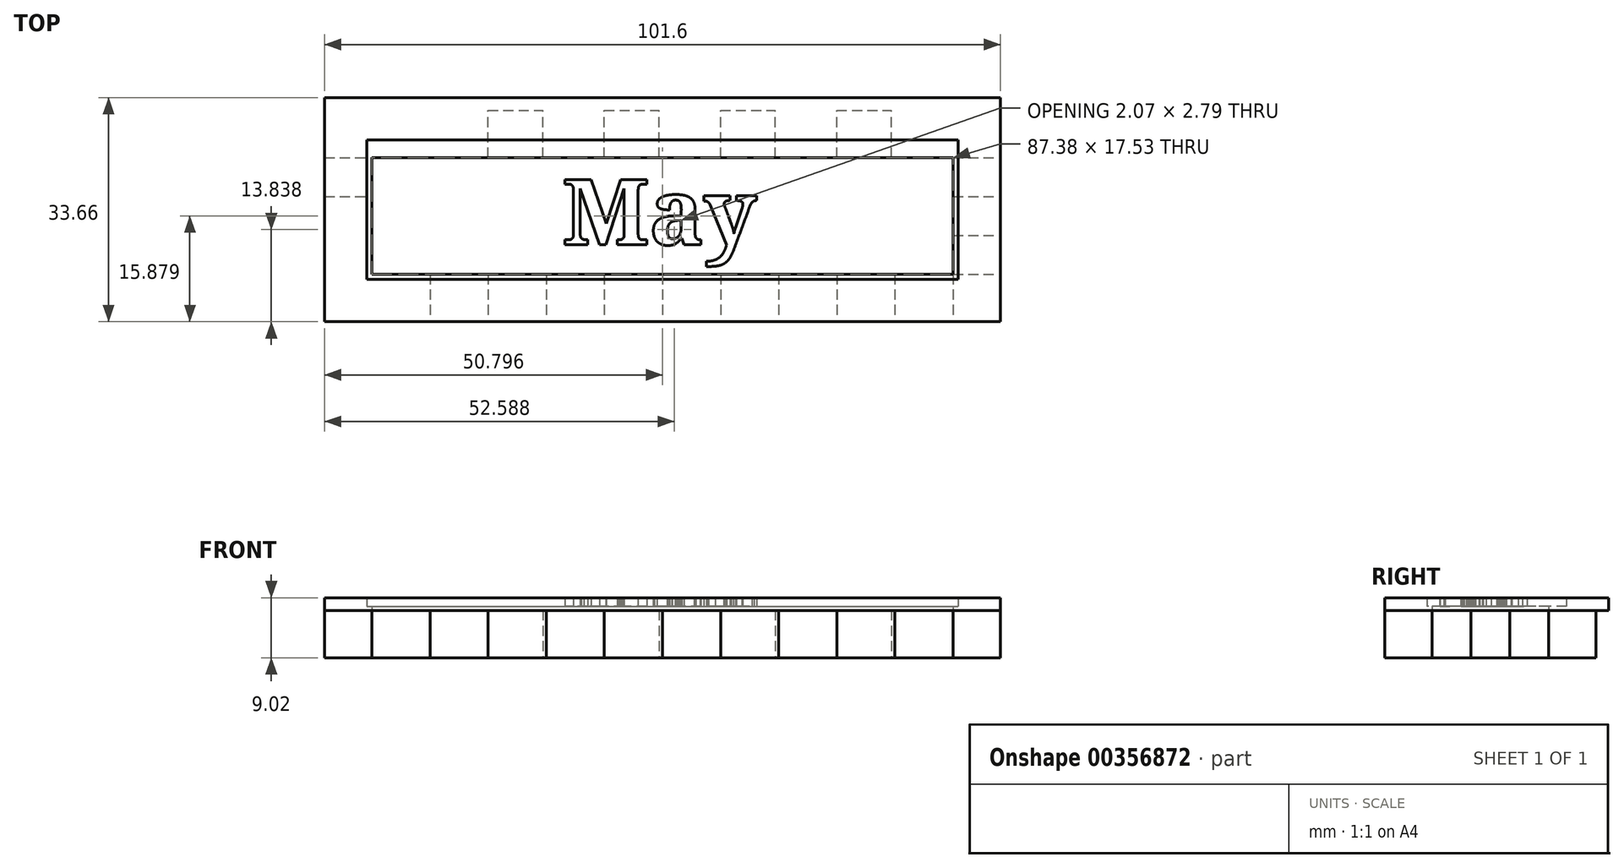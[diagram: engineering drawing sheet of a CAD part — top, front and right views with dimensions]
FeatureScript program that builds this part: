
annotation { "Feature Type Name" : "Feature", "Feature Type Description" : "" }
export const myFeature = defineFeature(function(context is Context, id is Id, definition is map)
    precondition{}
    {
        {
            var Q0;
            Q0=qCreatedBy(makeId("Top.planeOp"),FACE);
            var sketch = newSketch(context, id + "F0", { "sketchPlane" : qUnion([Q0])});
            skLineSegment(sketch, "E0.bottom", {"start": v(-52.12, 11.37) * mm, "end": v(49.48, 11.37) * mm});
            skLineSegment(sketch, "E0.top", {"start": v(-52.12, -20.38) * mm, "end": v(49.48, -20.38) * mm});
            skLineSegment(sketch, "E0.left", {"start": v(-52.12, 11.37) * mm, "end": v(-52.12, -20.38) * mm});
            skLineSegment(sketch, "E0.right", {"start": v(49.48, 11.37) * mm, "end": v(49.48, -20.38) * mm});
            skLineSegment(sketch, "E1.bottom", {"start": v(-52.12, 11.37) * mm, "end": v(-45.01, 11.37) * mm});
            skLineSegment(sketch, "E1.top", {"start": v(-52.12, 4.26) * mm, "end": v(-45.01, 4.26) * mm});
            skLineSegment(sketch, "E1.left", {"start": v(-52.12, 11.37) * mm, "end": v(-52.12, 4.26) * mm});
            skLineSegment(sketch, "E1.right", {"start": v(-45.01, 11.37) * mm, "end": v(-45.01, 4.26) * mm});
            skLineSegment(sketch, "E2.bottom", {"start": v(-45.01, 11.37) * mm, "end": v(-36.78, 11.37) * mm});
            skLineSegment(sketch, "E2.top", {"start": v(-45.01, 4.26) * mm, "end": v(-36.78, 4.26) * mm});
            skLineSegment(sketch, "E2.right", {"start": v(-36.78, 11.37) * mm, "end": v(-36.78, 4.26) * mm});
            skLineSegment(sketch, "E3.bottom", {"start": v(-36.78, 4.26) * mm, "end": v(-27.54, 4.26) * mm});
            skLineSegment(sketch, "E3.top", {"start": v(-36.78, 11.37) * mm, "end": v(-27.54, 11.37) * mm});
            skLineSegment(sketch, "E3.left", {"start": v(-36.78, 4.26) * mm, "end": v(-36.78, 11.37) * mm});
            skLineSegment(sketch, "E3.right", {"start": v(-27.54, 4.26) * mm, "end": v(-27.54, 11.37) * mm});
            skLineSegment(sketch, "E4.bottom", {"start": v(-27.54, 4.26) * mm, "end": v(-19.3, 4.26) * mm});
            skLineSegment(sketch, "E4.top", {"start": v(-27.54, 11.37) * mm, "end": v(-19.3, 11.37) * mm});
            skLineSegment(sketch, "E4.right", {"start": v(-19.3, 4.26) * mm, "end": v(-19.3, 11.37) * mm});
            skLineSegment(sketch, "E5.bottom", {"start": v(-19.3, 4.26) * mm, "end": v(-10.06, 4.26) * mm});
            skLineSegment(sketch, "E5.top", {"start": v(-19.3, 11.37) * mm, "end": v(-10.06, 11.37) * mm});
            skLineSegment(sketch, "E5.right", {"start": v(-10.06, 4.26) * mm, "end": v(-10.06, 11.37) * mm});
            skLineSegment(sketch, "E6.bottom", {"start": v(-10.06, 4.26) * mm, "end": v(-10.06, 4.26) * mm});
            skLineSegment(sketch, "E6.top", {"start": v(-10.06, 11.37) * mm, "end": v(-10.06, 11.37) * mm});
            skLineSegment(sketch, "E7.bottom", {"start": v(-10.06, 4.26) * mm, "end": v(-1.83, 4.26) * mm});
            skLineSegment(sketch, "E7.top", {"start": v(-10.06, 11.37) * mm, "end": v(-1.83, 11.37) * mm});
            skLineSegment(sketch, "E7.right", {"start": v(-1.83, 4.26) * mm, "end": v(-1.83, 11.37) * mm});
            skLineSegment(sketch, "E8.bottom", {"start": v(-1.83, 4.26) * mm, "end": v(7.41, 4.26) * mm});
            skLineSegment(sketch, "E8.top", {"start": v(-1.83, 11.37) * mm, "end": v(7.41, 11.37) * mm});
            skLineSegment(sketch, "E8.right", {"start": v(7.41, 4.26) * mm, "end": v(7.41, 11.37) * mm});
            skLineSegment(sketch, "E9.bottom", {"start": v(7.41, 4.26) * mm, "end": v(15.64, 4.26) * mm});
            skLineSegment(sketch, "E9.top", {"start": v(7.41, 11.37) * mm, "end": v(15.64, 11.37) * mm});
            skLineSegment(sketch, "E9.right", {"start": v(15.64, 4.26) * mm, "end": v(15.64, 11.37) * mm});
            skLineSegment(sketch, "E10.bottom", {"start": v(15.64, 4.26) * mm, "end": v(24.89, 4.26) * mm});
            skLineSegment(sketch, "E10.top", {"start": v(15.64, 11.37) * mm, "end": v(24.89, 11.37) * mm});
            skLineSegment(sketch, "E10.right", {"start": v(24.89, 4.26) * mm, "end": v(24.89, 11.37) * mm});
            skLineSegment(sketch, "E11.bottom", {"start": v(24.89, 4.26) * mm, "end": v(24.89, 4.26) * mm});
            skLineSegment(sketch, "E11.top", {"start": v(24.89, 11.37) * mm, "end": v(24.89, 11.37) * mm});
            skLineSegment(sketch, "E12.bottom", {"start": v(24.89, 4.26) * mm, "end": v(33.12, 4.26) * mm});
            skLineSegment(sketch, "E12.top", {"start": v(24.89, 11.37) * mm, "end": v(33.12, 11.37) * mm});
            skLineSegment(sketch, "E12.right", {"start": v(33.12, 4.26) * mm, "end": v(33.12, 11.37) * mm});
            skLineSegment(sketch, "E13.bottom", {"start": v(33.12, 4.26) * mm, "end": v(42.36, 4.26) * mm});
            skLineSegment(sketch, "E13.top", {"start": v(33.12, 11.37) * mm, "end": v(42.36, 11.37) * mm});
            skLineSegment(sketch, "E13.right", {"start": v(42.36, 4.26) * mm, "end": v(42.36, 11.37) * mm});
            skLineSegment(sketch, "E14.bottom", {"start": v(42.36, 4.26) * mm, "end": v(49.48, 4.26) * mm});
            skLineSegment(sketch, "E14.top", {"start": v(42.36, 11.37) * mm, "end": v(49.48, 11.37) * mm});
            skLineSegment(sketch, "E14.right", {"start": v(49.48, 4.26) * mm, "end": v(49.48, 11.37) * mm});
            skLineSegment(sketch, "E15.bottom", {"start": v(-52.12, -20.38) * mm, "end": v(-45.01, -20.38) * mm});
            skLineSegment(sketch, "E15.top", {"start": v(-52.12, -13.26) * mm, "end": v(-45.01, -13.26) * mm});
            skLineSegment(sketch, "E15.left", {"start": v(-52.12, -20.38) * mm, "end": v(-52.12, -13.26) * mm});
            skLineSegment(sketch, "E15.right", {"start": v(-45.01, -20.38) * mm, "end": v(-45.01, -13.26) * mm});
            skLineSegment(sketch, "E16.bottom", {"start": v(-45.01, -13.26) * mm, "end": v(-45.01, -13.26) * mm});
            skLineSegment(sketch, "E16.top", {"start": v(-45.01, -20.38) * mm, "end": v(-45.01, -20.38) * mm});
            skLineSegment(sketch, "E16.left", {"start": v(-45.01, -13.26) * mm, "end": v(-45.01, -20.38) * mm});
            skLineSegment(sketch, "E16.right", {"start": v(-45.01, -13.26) * mm, "end": v(-45.01, -20.38) * mm});
            skLineSegment(sketch, "E17.bottom", {"start": v(-45.01, -13.26) * mm, "end": v(-36.27, -13.26) * mm});
            skLineSegment(sketch, "E17.top", {"start": v(-45.01, -20.38) * mm, "end": v(-36.27, -20.38) * mm});
            skLineSegment(sketch, "E17.right", {"start": v(-36.27, -13.26) * mm, "end": v(-36.27, -20.38) * mm});
            skLineSegment(sketch, "E18.bottom", {"start": v(-36.27, -13.26) * mm, "end": v(-36.27, -13.26) * mm});
            skLineSegment(sketch, "E18.top", {"start": v(-36.27, -20.38) * mm, "end": v(-36.27, -20.38) * mm});
            skLineSegment(sketch, "E19.bottom", {"start": v(-36.27, -13.26) * mm, "end": v(-27.54, -13.26) * mm});
            skLineSegment(sketch, "E19.top", {"start": v(-36.27, -20.38) * mm, "end": v(-27.54, -20.38) * mm});
            skLineSegment(sketch, "E19.right", {"start": v(-27.54, -13.26) * mm, "end": v(-27.54, -20.38) * mm});
            skLineSegment(sketch, "E20.bottom", {"start": v(-27.54, -13.26) * mm, "end": v(-18.8, -13.26) * mm});
            skLineSegment(sketch, "E20.top", {"start": v(-27.54, -20.38) * mm, "end": v(-18.8, -20.38) * mm});
            skLineSegment(sketch, "E20.right", {"start": v(-18.8, -13.26) * mm, "end": v(-18.8, -20.38) * mm});
            skLineSegment(sketch, "E21.bottom", {"start": v(-18.8, -13.26) * mm, "end": v(-10.06, -13.26) * mm});
            skLineSegment(sketch, "E21.top", {"start": v(-18.8, -20.38) * mm, "end": v(-10.06, -20.38) * mm});
            skLineSegment(sketch, "E21.right", {"start": v(-10.06, -13.26) * mm, "end": v(-10.06, -20.38) * mm});
            skLineSegment(sketch, "E22.bottom", {"start": v(-10.06, -13.26) * mm, "end": v(-1.32, -13.26) * mm});
            skLineSegment(sketch, "E22.top", {"start": v(-10.06, -20.38) * mm, "end": v(-1.32, -20.38) * mm});
            skLineSegment(sketch, "E22.right", {"start": v(-1.32, -13.26) * mm, "end": v(-1.32, -20.38) * mm});
            skLineSegment(sketch, "E23.bottom", {"start": v(-1.32, -13.26) * mm, "end": v(7.41, -13.26) * mm});
            skLineSegment(sketch, "E23.top", {"start": v(-1.32, -20.38) * mm, "end": v(7.41, -20.38) * mm});
            skLineSegment(sketch, "E23.right", {"start": v(7.41, -13.26) * mm, "end": v(7.41, -20.38) * mm});
            skLineSegment(sketch, "E24.bottom", {"start": v(7.41, -13.26) * mm, "end": v(16.15, -13.26) * mm});
            skLineSegment(sketch, "E24.top", {"start": v(7.41, -20.38) * mm, "end": v(16.15, -20.38) * mm});
            skLineSegment(sketch, "E24.right", {"start": v(16.15, -13.26) * mm, "end": v(16.15, -20.38) * mm});
            skLineSegment(sketch, "E25.bottom", {"start": v(16.15, -13.26) * mm, "end": v(24.89, -13.26) * mm});
            skLineSegment(sketch, "E25.top", {"start": v(16.15, -20.38) * mm, "end": v(24.89, -20.38) * mm});
            skLineSegment(sketch, "E25.right", {"start": v(24.89, -13.26) * mm, "end": v(24.89, -20.38) * mm});
            skLineSegment(sketch, "E26.bottom", {"start": v(24.89, -13.26) * mm, "end": v(33.63, -13.26) * mm});
            skLineSegment(sketch, "E26.top", {"start": v(24.89, -20.38) * mm, "end": v(33.63, -20.38) * mm});
            skLineSegment(sketch, "E26.right", {"start": v(33.63, -13.26) * mm, "end": v(33.63, -20.38) * mm});
            skLineSegment(sketch, "E27.bottom", {"start": v(33.63, -13.26) * mm, "end": v(42.36, -13.26) * mm});
            skLineSegment(sketch, "E27.top", {"start": v(33.63, -20.38) * mm, "end": v(42.36, -20.38) * mm});
            skLineSegment(sketch, "E27.right", {"start": v(42.36, -13.26) * mm, "end": v(42.36, -20.38) * mm});
            skLineSegment(sketch, "E28.bottom", {"start": v(42.36, -13.26) * mm, "end": v(49.48, -13.26) * mm});
            skLineSegment(sketch, "E28.top", {"start": v(42.36, -20.38) * mm, "end": v(49.48, -20.38) * mm});
            skLineSegment(sketch, "E28.right", {"start": v(49.48, -13.26) * mm, "end": v(49.48, -20.38) * mm});
            skLineSegment(sketch, "E29.top", {"start": v(-52.12, -1.58) * mm, "end": v(-45.01, -1.58) * mm});
            skLineSegment(sketch, "E29.left", {"start": v(-52.12, 4.26) * mm, "end": v(-52.12, -1.58) * mm});
            skLineSegment(sketch, "E29.right", {"start": v(-45.01, 4.26) * mm, "end": v(-45.01, -1.58) * mm});
            skLineSegment(sketch, "E30.top", {"start": v(-52.12, -7.42) * mm, "end": v(-45.01, -7.42) * mm});
            skLineSegment(sketch, "E30.left", {"start": v(-52.12, -1.58) * mm, "end": v(-52.12, -7.42) * mm});
            skLineSegment(sketch, "E30.right", {"start": v(-45.01, -1.58) * mm, "end": v(-45.01, -7.42) * mm});
            skLineSegment(sketch, "E31.bottom", {"start": v(-45.01, -7.42) * mm, "end": v(-52.12, -7.42) * mm});
            skLineSegment(sketch, "E31.top", {"start": v(-45.01, -13.26) * mm, "end": v(-52.12, -13.26) * mm});
            skLineSegment(sketch, "E31.left", {"start": v(-45.01, -7.42) * mm, "end": v(-45.01, -13.26) * mm});
            skLineSegment(sketch, "E31.right", {"start": v(-52.12, -7.42) * mm, "end": v(-52.12, -13.26) * mm});
            skLineSegment(sketch, "E32.top", {"start": v(42.36, -1.58) * mm, "end": v(49.48, -1.58) * mm});
            skLineSegment(sketch, "E32.left", {"start": v(42.36, 4.26) * mm, "end": v(42.36, -1.58) * mm});
            skLineSegment(sketch, "E32.right", {"start": v(49.48, 4.26) * mm, "end": v(49.48, -1.58) * mm});
            skLineSegment(sketch, "E33.top", {"start": v(42.36, -7.42) * mm, "end": v(49.48, -7.42) * mm});
            skLineSegment(sketch, "E33.left", {"start": v(42.36, -1.58) * mm, "end": v(42.36, -7.42) * mm});
            skLineSegment(sketch, "E33.right", {"start": v(49.48, -1.58) * mm, "end": v(49.48, -7.42) * mm});
            skLineSegment(sketch, "E34.left", {"start": v(42.36, -7.42) * mm, "end": v(42.36, -13.26) * mm});
            skLineSegment(sketch, "E34.right", {"start": v(49.48, -7.42) * mm, "end": v(49.48, -13.26) * mm});
            skSolve(sketch);
        }
        {
            var Q0;
            Q0=makeQuery(id+"F0.imprint","IMPRINT",FACE,{"disambiguationData":[TD([[makeQuery(id+"F0.imprint","IMPRINT",EDGE,{"derivedFrom":sQuery(id+"F0.wireOp",EDGE,"E2.top")}),-1.0]])]});
            var Q1;
            Q1=makeQuery(id+"F0.imprint","IMPRINT",FACE,{"disambiguationData":[TD([[makeQuery(id+"F0.imprint","IMPRINT",EDGE,{"derivedFrom":sQuery(id+"F0.wireOp",EDGE,"E2.bottom")}),-1.0]])]});
            var Q2;
            Q2=makeQuery(id+"F0.imprint","IMPRINT",FACE,{"disambiguationData":[TD([[makeQuery(id+"F0.imprint","IMPRINT",EDGE,{"derivedFrom":sQuery(id+"F0.wireOp",EDGE,"E4.bottom")}),1.0]])]});
            var Q3;
            Q3=makeQuery(id+"F0.imprint","IMPRINT",FACE,{"disambiguationData":[TD([[makeQuery(id+"F0.imprint","IMPRINT",EDGE,{"derivedFrom":sQuery(id+"F0.wireOp",EDGE,"E7.bottom")}),1.0]])]});
            var Q4;
            Q4=makeQuery(id+"F0.imprint","IMPRINT",FACE,{"disambiguationData":[TD([[makeQuery(id+"F0.imprint","IMPRINT",EDGE,{"derivedFrom":sQuery(id+"F0.wireOp",EDGE,"E9.bottom")}),1.0]])]});
            var Q5;
            Q5=makeQuery(id+"F0.imprint","IMPRINT",FACE,{"disambiguationData":[TD([[makeQuery(id+"F0.imprint","IMPRINT",EDGE,{"derivedFrom":sQuery(id+"F0.wireOp",EDGE,"E12.bottom")}),1.0]])]});
            var Q6;
            Q6=makeQuery(id+"F0.imprint","IMPRINT",FACE,{"disambiguationData":[TD([[makeQuery(id+"F0.imprint","IMPRINT",EDGE,{"derivedFrom":sQuery(id+"F0.wireOp",EDGE,"E14.bottom")}),-1.0]])]});
            var Q7;
            Q7=makeQuery(id+"F0.imprint","IMPRINT",FACE,{"disambiguationData":[TD([[makeQuery(id+"F0.imprint","IMPRINT",EDGE,{"derivedFrom":sQuery(id+"F0.wireOp",EDGE,"E33.top")}),-1.0]])]});
            var Q8;
            Q8=makeQuery(id+"F0.imprint","IMPRINT",FACE,{"disambiguationData":[TD([[makeQuery(id+"F0.imprint","IMPRINT",EDGE,{"derivedFrom":sQuery(id+"F0.wireOp",EDGE,"E27.bottom")}),-1.0]])]});
            var Q9;
            Q9=makeQuery(id+"F0.imprint","IMPRINT",FACE,{"disambiguationData":[TD([[makeQuery(id+"F0.imprint","IMPRINT",EDGE,{"derivedFrom":sQuery(id+"F0.wireOp",EDGE,"E25.bottom")}),-1.0]])]});
            var Q10;
            Q10=makeQuery(id+"F0.imprint","IMPRINT",FACE,{"disambiguationData":[TD([[makeQuery(id+"F0.imprint","IMPRINT",EDGE,{"derivedFrom":sQuery(id+"F0.wireOp",EDGE,"E23.bottom")}),-1.0]])]});
            var Q11;
            Q11=makeQuery(id+"F0.imprint","IMPRINT",FACE,{"disambiguationData":[TD([[makeQuery(id+"F0.imprint","IMPRINT",EDGE,{"derivedFrom":sQuery(id+"F0.wireOp",EDGE,"E21.bottom")}),-1.0]])]});
            var Q12;
            Q12=makeQuery(id+"F0.imprint","IMPRINT",FACE,{"disambiguationData":[TD([[makeQuery(id+"F0.imprint","IMPRINT",EDGE,{"derivedFrom":sQuery(id+"F0.wireOp",EDGE,"E19.bottom")}),-1.0]])]});
            var Q13;
            Q13=makeQuery(id+"F0.imprint","IMPRINT",FACE,{"disambiguationData":[TD([[makeQuery(id+"F0.imprint","IMPRINT",EDGE,{"derivedFrom":sQuery(id+"F0.wireOp",EDGE,"E31.bottom")}),1.0]])]});
            var Q14;
            Q14=makeQuery(id+"F0.imprint","IMPRINT",FACE,{"disambiguationData":[TD([[makeQuery(id+"F0.imprint","IMPRINT",EDGE,{"derivedFrom":sQuery(id+"F0.wireOp",EDGE,"E1.top")}),-1.0]])]});
            extrude(context, id + "F1", {"entities" : qUnion([Q0, Q1, Q2, Q3, Q4, Q5, Q6, Q7, Q8, Q9, Q10, Q11, Q12, Q13, Q14]), "depth" : 7.11 * mm});
        }
        {
            var Q0;
            Q0=makeQuery(id+"F1.opExtrude","CAP_FACE",FACE,{"disambiguationData":[OSD([sQuery(id+"F0.wireOp",EDGE,"E2.bottom"),sQuery(id+"F0.wireOp",EDGE,"E1.right"),sQuery(id+"F0.wireOp",EDGE,"E3.bottom"),sQuery(id+"F0.wireOp",EDGE,"E3.left"),sQuery(id+"F0.wireOp",EDGE,"E4.top"),sQuery(id+"F0.wireOp",EDGE,"E3.right"),sQuery(id+"F0.wireOp",EDGE,"E5.bottom"),sQuery(id+"F0.wireOp",EDGE,"E4.right"),sQuery(id+"F0.wireOp",EDGE,"E6.top"),sQuery(id+"F0.wireOp",EDGE,"E5.right"),sQuery(id+"F0.wireOp",EDGE,"E7.bottom"),sQuery(id+"F0.wireOp",EDGE,"E5.right"),sQuery(id+"F0.wireOp",EDGE,"E8.top"),sQuery(id+"F0.wireOp",EDGE,"E7.right"),sQuery(id+"F0.wireOp",EDGE,"E9.bottom"),sQuery(id+"F0.wireOp",EDGE,"E8.right"),sQuery(id+"F0.wireOp",EDGE,"E10.top"),sQuery(id+"F0.wireOp",EDGE,"E9.right"),sQuery(id+"F0.wireOp",EDGE,"E11.bottom"),sQuery(id+"F0.wireOp",EDGE,"E10.right"),sQuery(id+"F0.wireOp",EDGE,"E12.top"),sQuery(id+"F0.wireOp",EDGE,"E10.right"),sQuery(id+"F0.wireOp",EDGE,"E13.bottom"),sQuery(id+"F0.wireOp",EDGE,"E12.right"),sQuery(id+"F0.wireOp",EDGE,"E16.bottom"),sQuery(id+"F0.wireOp",EDGE,"E17.top"),sQuery(id+"F0.wireOp",EDGE,"E16.left"),sQuery(id+"F0.wireOp",EDGE,"E18.bottom"),sQuery(id+"F0.wireOp",EDGE,"E17.right"),sQuery(id+"F0.wireOp",EDGE,"E19.top"),sQuery(id+"F0.wireOp",EDGE,"E17.right"),sQuery(id+"F0.wireOp",EDGE,"E20.bottom"),sQuery(id+"F0.wireOp",EDGE,"E19.right"),sQuery(id+"F0.wireOp",EDGE,"E21.top"),sQuery(id+"F0.wireOp",EDGE,"E20.right"),sQuery(id+"F0.wireOp",EDGE,"E22.bottom"),sQuery(id+"F0.wireOp",EDGE,"E21.right"),sQuery(id+"F0.wireOp",EDGE,"E23.top"),sQuery(id+"F0.wireOp",EDGE,"E22.right"),sQuery(id+"F0.wireOp",EDGE,"E24.bottom"),sQuery(id+"F0.wireOp",EDGE,"E23.right"),sQuery(id+"F0.wireOp",EDGE,"E25.top"),sQuery(id+"F0.wireOp",EDGE,"E24.right"),sQuery(id+"F0.wireOp",EDGE,"E26.bottom"),sQuery(id+"F0.wireOp",EDGE,"E25.right"),sQuery(id+"F0.wireOp",EDGE,"E27.top"),sQuery(id+"F0.wireOp",EDGE,"E26.right"),sQuery(id+"F0.wireOp",EDGE,"E27.right"),sQuery(id+"F0.wireOp",EDGE,"E1.top"),sQuery(id+"F0.wireOp",EDGE,"E29.left"),sQuery(id+"F0.wireOp",EDGE,"E29.top"),sQuery(id+"F0.wireOp",EDGE,"E30.right"),sQuery(id+"F0.wireOp",EDGE,"E31.bottom"),sQuery(id+"F0.wireOp",EDGE,"E31.top"),sQuery(id+"F0.wireOp",EDGE,"E31.right"),sQuery(id+"F0.wireOp",EDGE,"E14.bottom"),sQuery(id+"F0.wireOp",EDGE,"E32.right"),sQuery(id+"F0.wireOp",EDGE,"E32.top"),sQuery(id+"F0.wireOp",EDGE,"E33.left"),sQuery(id+"F0.wireOp",EDGE,"E33.top"),sQuery(id+"F0.wireOp",EDGE,"E28.bottom"),sQuery(id+"F0.wireOp",EDGE,"E34.right")])],"isStart":false});
            var sketch = newSketch(context, id + "F2", { "sketchPlane" : qUnion([Q0])});
            skLineSegment(sketch, "E35.bottom", {"start": v(-52.12, -20.38) * mm, "end": v(-45.01, -20.38) * mm});
            skLineSegment(sketch, "E35.top", {"start": v(-52.12, 13.28) * mm, "end": v(-45.01, 13.28) * mm});
            skLineSegment(sketch, "E35.left", {"start": v(-52.12, -20.38) * mm, "end": v(-52.12, 13.28) * mm});
            skLineSegment(sketch, "E35.right", {"start": v(-45.01, -20.38) * mm, "end": v(-45.01, 13.28) * mm});
            skLineSegment(sketch, "E36.bottom", {"start": v(-52.12, -20.38) * mm, "end": v(49.48, -20.38) * mm});
            skLineSegment(sketch, "E36.top", {"start": v(-52.12, -13.26) * mm, "end": v(49.48, -13.26) * mm});
            skLineSegment(sketch, "E36.left", {"start": v(-52.12, -20.38) * mm, "end": v(-52.12, -13.26) * mm});
            skLineSegment(sketch, "E36.right", {"start": v(49.48, -20.38) * mm, "end": v(49.48, -13.26) * mm});
            skPoint(sketch, "E37.oppositeSnap0", {"position": v(42.36, -4.5) * mm});
            skLineSegment(sketch, "E37.bottom", {"start": v(49.48, -20.38) * mm, "end": v(42.36, -20.38) * mm});
            skLineSegment(sketch, "E37.top", {"start": v(49.48, 13.28) * mm, "end": v(42.36, 13.28) * mm});
            skLineSegment(sketch, "E37.left", {"start": v(49.48, -20.38) * mm, "end": v(49.48, 13.28) * mm});
            skLineSegment(sketch, "E37.right", {"start": v(42.36, -20.38) * mm, "end": v(42.36, 13.28) * mm});
            skLineSegment(sketch, "E38.bottom", {"start": v(-52.12, 13.28) * mm, "end": v(49.48, 13.28) * mm});
            skLineSegment(sketch, "E38.top", {"start": v(-52.12, 4.26) * mm, "end": v(49.48, 4.26) * mm});
            skLineSegment(sketch, "E38.left", {"start": v(-52.12, 13.28) * mm, "end": v(-52.12, 4.26) * mm});
            skLineSegment(sketch, "E38.right", {"start": v(49.48, 13.28) * mm, "end": v(49.48, 4.26) * mm});
            skSolve(sketch);
        }
        {
            var Q0;
            Q0=qSketchRegion(id+"F2",true);
            var Q1;
            {var subQ5=sQuery(id+"F2.wireOp",EDGE,"E36.top");var subQ10=sQuery(id+"F2.wireOp",EDGE,"E35.right");var subQ12=makeQuery(id+"F2.imprint","INTERSECT",VERTEX,{"derivedFrom":[makeQuery(id+"F1.opExtrude","CAP_EDGE",EDGE,{"disambiguationData":[OSD([sQuery(id+"F0.wireOp",EDGE,"E31.bottom")])],"isStart":false}),subQ10]});var subQ24=makeQuery(id+"F2.imprint","INTERSECT",VERTEX,{"derivedFrom":[subQ10,subQ5]});Q1=makeQuery(id+"F2.imprint","IMPRINT",FACE,{"disambiguationData":[TD([[makeQuery(id+"F2.imprint","IMPRINT",EDGE,{"disambiguationData":[TD([[subQ12,1.0],[subQ24,-1.0]])],"derivedFrom":subQ10}),-1.0]])]});}
            extrude(context, id + "F3", {"entities" : qUnion([Q0, Q1]), "depth" : 0.64 * mm});
        }
        {
            var Q0;
            Q0=makeQuery(id+"F3.opExtrude","CAP_FACE",FACE,{"disambiguationData":[OSD([sQuery(id+"F2.wireOp",EDGE,"E35.left"),sQuery(id+"F2.wireOp",EDGE,"E36.bottom"),sQuery(id+"F2.wireOp",EDGE,"E36.left"),sQuery(id+"F2.wireOp",EDGE,"E37.bottom"),sQuery(id+"F2.wireOp",EDGE,"E37.left"),sQuery(id+"F2.wireOp",EDGE,"E38.bottom"),sQuery(id+"F2.wireOp",EDGE,"E38.left"),sQuery(id+"F2.wireOp",EDGE,"E38.right")])],"isStart":false});
            var sketch = newSketch(context, id + "F4", { "sketchPlane" : qUnion([Q0])});
            skLineSegment(sketch, "E39.bottom", {"start": v(-52.12, 13.28) * mm, "end": v(49.48, 13.28) * mm});
            skLineSegment(sketch, "E39.top", {"start": v(-52.12, 6.93) * mm, "end": v(49.48, 6.93) * mm});
            skLineSegment(sketch, "E39.left", {"start": v(-52.12, 13.28) * mm, "end": v(-52.12, 6.93) * mm});
            skLineSegment(sketch, "E39.right", {"start": v(49.48, 13.28) * mm, "end": v(49.48, 6.93) * mm});
            skLineSegment(sketch, "E40.bottom", {"start": v(-52.12, 13.28) * mm, "end": v(-45.77, 13.28) * mm});
            skLineSegment(sketch, "E40.top", {"start": v(-52.12, -20.38) * mm, "end": v(-45.77, -20.38) * mm});
            skLineSegment(sketch, "E40.left", {"start": v(-52.12, 13.28) * mm, "end": v(-52.12, -20.38) * mm});
            skLineSegment(sketch, "E40.right", {"start": v(-45.77, 13.28) * mm, "end": v(-45.77, -20.38) * mm});
            skLineSegment(sketch, "E41.bottom", {"start": v(-52.12, -14.03) * mm, "end": v(49.48, -14.03) * mm});
            skLineSegment(sketch, "E41.top", {"start": v(-52.12, -20.38) * mm, "end": v(49.48, -20.38) * mm});
            skLineSegment(sketch, "E41.left", {"start": v(-52.12, -14.03) * mm, "end": v(-52.12, -20.38) * mm});
            skLineSegment(sketch, "E41.right", {"start": v(49.48, -14.03) * mm, "end": v(49.48, -20.38) * mm});
            skLineSegment(sketch, "E42.bottom", {"start": v(49.48, -20.38) * mm, "end": v(43.13, -20.38) * mm});
            skLineSegment(sketch, "E42.top", {"start": v(49.48, 13.28) * mm, "end": v(43.13, 13.28) * mm});
            skLineSegment(sketch, "E42.left", {"start": v(49.48, -20.38) * mm, "end": v(49.48, 13.28) * mm});
            skLineSegment(sketch, "E42.right", {"start": v(43.13, -20.38) * mm, "end": v(43.13, 13.28) * mm});
            skSolve(sketch);
        }
        {
            var Q0;
            Q0=qSketchRegion(id+"F4",true);
            extrude(context, id + "F5", {"entities" : qUnion([Q0]), "operationType" : NewBodyOperationType.ADD, "depth" : 1.27 * mm});
        }
        {
            var Q0;
            Q0=makeQuery(id+"F3.opExtrude","CAP_FACE",FACE,{"disambiguationData":[OSD([sQuery(id+"F2.wireOp",EDGE,"E35.left"),sQuery(id+"F2.wireOp",EDGE,"E36.bottom"),sQuery(id+"F2.wireOp",EDGE,"E36.left"),sQuery(id+"F2.wireOp",EDGE,"E37.bottom"),sQuery(id+"F2.wireOp",EDGE,"E37.left"),sQuery(id+"F2.wireOp",EDGE,"E38.bottom"),sQuery(id+"F2.wireOp",EDGE,"E38.left"),sQuery(id+"F2.wireOp",EDGE,"E38.right")])],"isStart":false});
            var sketch = newSketch(context, id + "F6", { "sketchPlane" : qUnion([Q0])});
            skText(sketch, "E43", { "text": "May", "fontName": "NotoSerif-Bold.ttf"});
            const initialGuessF6  = {"E43": [-0.01638, -0.0088, 1, 0, 0.00988]};
            skSetInitialGuess(sketch, initialGuessF6);
            skSolve(sketch);
        }
        {
            var Q0;
            Q0 = qSketchRegion(id + "F6", true);
            extrude(context, id + "F7", {"entities" : qUnion([Q0]), "operationType" : NewBodyOperationType.ADD, "depth" : 1.27 * mm});
        }
    });
